# Revit family: Shower-Valve_Trim-KALLISTA-Vir_Stil-P80242
name_source: partatom
category: Specialty Equipment
units: mm (PartAtom-declared; Revit-internal decimal feet)

## family parameters
Cut with Voids When Loaded = No
Host = Face
OmniClass Number = 23.31.17.00
OmniClass Title = Showers
Part Type = Normal
Room Calculation Point = No
Round Connector Dimension = Use Diameter
Shared = No

## types (4) — shared parameters
ADA Compliant = No
Assembly Code = D2010700
CW Connection = No
Cold Water Inlet = Cold Water Inlet
Date Modified = 10/14/2023
Default Elevation = 42"
Description = Transfer Trim, Lever Handle
Drain Included = No
HW Connection = No
Handle Clearance = 2 7/8"
Height = 3 3/4"
Hot Water Inlet = Hot Water Inlet
Length = 3 5/16"
Manufacturer = Kallista Co.
Master Format 2014 = 22 42 23
Master Format 2014 Name = Residential Showers
Material = Premium Metal Construction
Product Name = Vir Stil
Tempered Water Inlet = Tempered Water Inlet
URL = https://www.kallista.com
Vent Connection = No
Waste Connection = No
Waste Water Outlet = Waste Water Outlet
WaterSense Certified = No
Width = 3 3/4"

## per-type parameters (varying)
| type | Finish | Model | Type |
| BAF-Brushed French Gold | Kallista-Metal-BAF-Brushed_French_Gold | P80242-LV-BAF | 1 |
| BN-Brushed Nickel | Kallista-Metal-BN-Brushed_Nickel | P80242-LV-BN | 2 |
| SN-Polished Nickel | Kallista-Metal-SN-Polished_Nickel | P80242-LV-SN | 4 |
| CP-Chrome | Kallista-Metal-CP-Chrome | P80242-LV-CP | 3 |

## geometry (parser evidence)
native form markers: Sweep x5
no freeform markers — native parametric forms only
